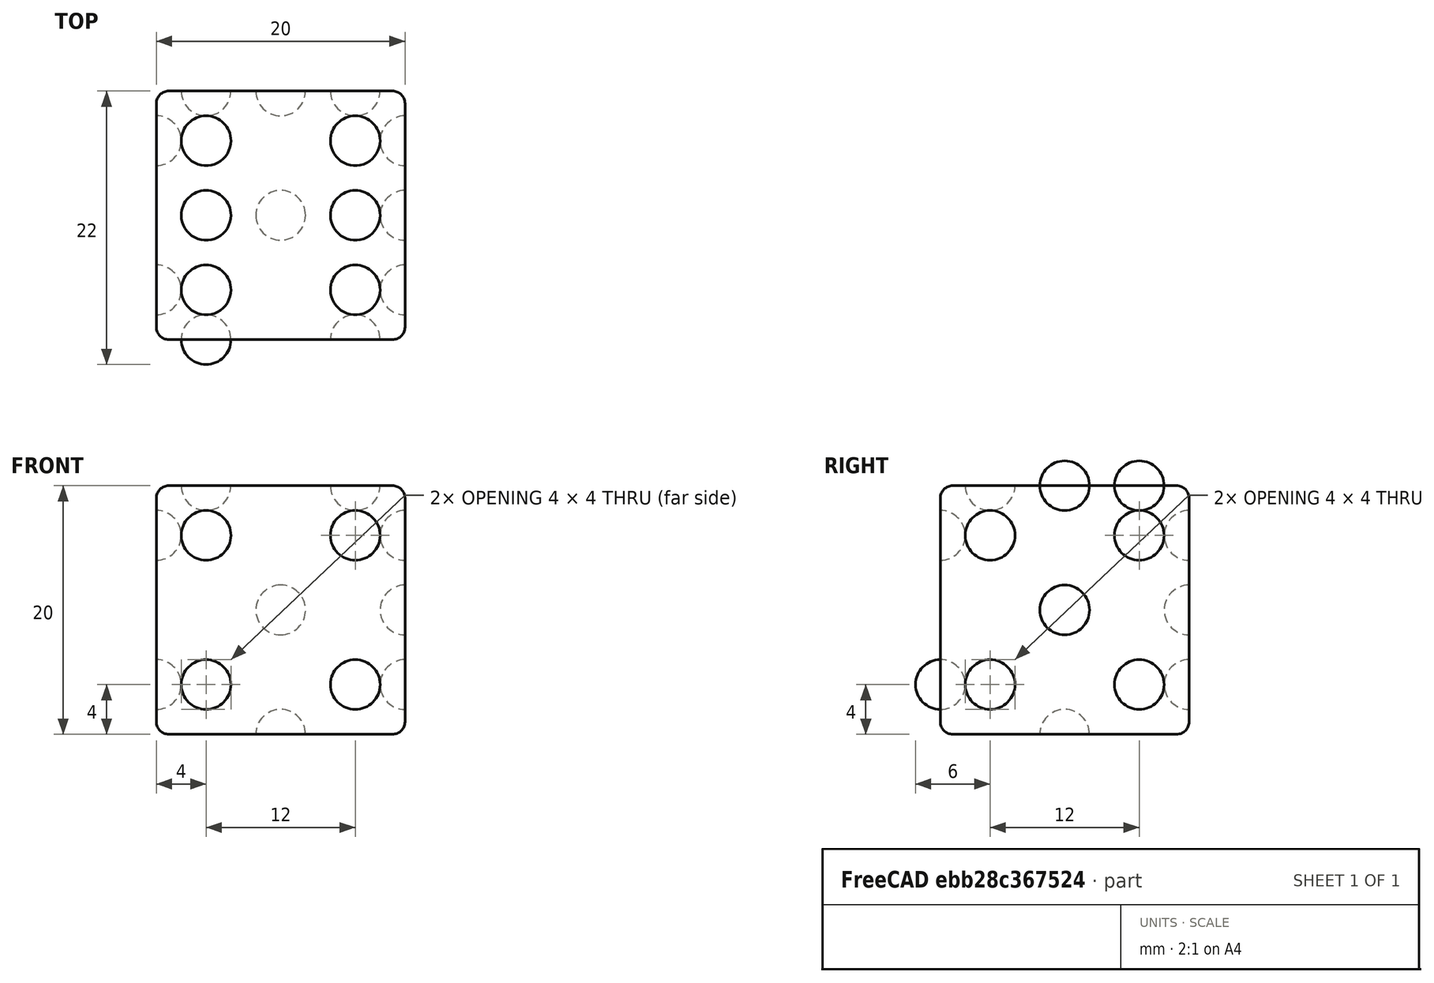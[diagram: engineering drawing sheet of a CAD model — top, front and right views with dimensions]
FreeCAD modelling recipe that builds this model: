
FCSTD DOCUMENT  (FreeCAD 1.0R39319 (Git))
Label: ojt1_t13r02_dado
License: All rights reserved
LicenseURL: https://en.wikipedia.org/wiki/All_rights_reserved
objects: Part::FeaturePython×12, Part::Sphere×10, Part::Cut×10, Part::MultiFuse×4, App::DocumentObjectGroup×3, Part::Box×1, Part::Fillet×1
note: 32 computed .brp shape members not serialized (recipe doc carries the construction recipe); baked Part::Feature solids carry a one-line shape summary decoded from their .brp

FEATURE [Part::Box] Box  label="Cube"
  AttacherType = Attacher::AttachEngine3D
  Height = 20
  Length = 20
  Width = 20
FEATURE [Part::Sphere] Sphere
  Angle1 = -90
  Angle2 = 90
  Angle3 = 360
  AttacherType = Attacher::AttachEngine3D
  Placement = pos=(4,0,4) rot=(0,0,1;0rad)
  Radius = 2
FEATURE [Part::FeaturePython] Array  # Draft array (typed FeaturePython)
  AlwaysSyncPlacement = false
  Angle = 360
  ArrayType = 0
  Axis = (0,0,1)
  Base = -> Sphere
  Center = (0,0,0)
  Count = 6
  ExpandArray = false
  Fuse = false
  IntervalAxis = (0,0,0)
  IntervalX = (6,0,0)
  IntervalY = (0,12,0)
  IntervalZ = (0,0,12)
  NumberCircles = 3
  NumberPolar = 5
  NumberX = 3
  NumberY = 1
  NumberZ = 2
  Placement = pos=(20,20,20) rot=(-0.57735,0.57735,0.57735;4.18879rad)
  PlacementList = 6 placements: [(4,0,4),(4,0,16),(10,0,4),(10,0,16),(16,0,4),(16,0,16)]
  RadialDistance = 50
  ScaleList = (6) [(1,1,1),(1,1,1),(1,1,1),(1,1,1),(1,1,1),(1,1,1)]
  Symmetry = 1
  TangentialDistance = 25
FEATURE [Part::Sphere] Sphere003
  Angle1 = -90
  Angle2 = 90
  Angle3 = 360
  AttacherType = Attacher::AttachEngine3D
  Placement = pos=(4,0,4) rot=(0,0,1;0rad)
  Radius = 2
FEATURE [Part::FeaturePython] Array002  # Draft array (typed FeaturePython)
  AlwaysSyncPlacement = false
  Angle = 360
  ArrayType = 0
  Axis = (0,0,1)
  Base = -> Sphere003
  Center = (0,0,0)
  Count = 4
  ExpandArray = false
  Fuse = false
  IntervalAxis = (0,0,0)
  IntervalX = (12,0,0)
  IntervalY = (0,12,0)
  IntervalZ = (0,0,12)
  NumberCircles = 3
  NumberPolar = 5
  NumberX = 2
  NumberY = 1
  NumberZ = 2
  PlacementList = 4 placements: [(4,0,4),(4,0,16),(16,0,4),(16,0,16)]
  RadialDistance = 50
  ScaleList = (4) [(1,1,1),(1,1,1),(1,1,1),(1,1,1)]
  Symmetry = 1
  TangentialDistance = 25
FEATURE [Part::Sphere] Sphere004
  Angle1 = -90
  Angle2 = 90
  Angle3 = 360
  AttacherType = Attacher::AttachEngine3D
  Placement = pos=(4,0,4) rot=(0,0,1;0rad)
  Radius = 2
FEATURE [Part::FeaturePython] Array003  # Draft array (typed FeaturePython)
  AlwaysSyncPlacement = false
  Angle = 360
  ArrayType = 0
  Axis = (0,0,1)
  Base = -> Sphere004
  Center = (0,0,0)
  Count = 4
  ExpandArray = false
  Fuse = false
  IntervalAxis = (0,0,0)
  IntervalX = (12,0,0)
  IntervalY = (0,12,0)
  IntervalZ = (0,0,12)
  NumberCircles = 3
  NumberPolar = 5
  NumberX = 2
  NumberY = 1
  NumberZ = 2
  Placement = pos=(0,0,0) rot=(0,0,1;1.5708rad)
  PlacementList = 4 placements: [(4,0,4),(4,0,16),(16,0,4),(16,0,16)]
  RadialDistance = 50
  ScaleList = (4) [(1,1,1),(1,1,1),(1,1,1),(1,1,1)]
  Symmetry = 1
  TangentialDistance = 25
FEATURE [Part::Sphere] Sphere009
  Angle1 = -90
  Angle2 = 90
  Angle3 = 360
  AttacherType = Attacher::AttachEngine3D
  Placement = pos=(0,10,10) rot=(0,0,1;0rad)
  Radius = 2
FEATURE [Part::Sphere] Sphere001
  Angle1 = -90
  Angle2 = 90
  Angle3 = 360
  AttacherType = Attacher::AttachEngine3D
  Placement = pos=(4,0,4) rot=(0,0,1;0rad)
  Radius = 2
FEATURE [Part::FeaturePython] Array001  # Draft array (typed FeaturePython)
  AlwaysSyncPlacement = false
  Angle = 360
  ArrayType = 0
  Axis = (0,0,1)
  Base = -> Sphere001
  Center = (0,0,0)
  Count = 4
  ExpandArray = false
  Fuse = false
  IntervalAxis = (0,0,0)
  IntervalX = (12,0,0)
  IntervalY = (0,12,0)
  IntervalZ = (0,0,12)
  NumberCircles = 3
  NumberPolar = 5
  NumberX = 2
  NumberY = 1
  NumberZ = 2
  Placement = pos=(0,0,0) rot=(0,0,1;1.5708rad)
  PlacementList = 4 placements: [(4,0,4),(4,0,16),(16,0,4),(16,0,16)]
  RadialDistance = 50
  ScaleList = (4) [(1,1,1),(1,1,1),(1,1,1),(1,1,1)]
  Symmetry = 1
  TangentialDistance = 25
FEATURE [Part::Sphere] Sphere002
  Angle1 = -90
  Angle2 = 90
  Angle3 = 360
  AttacherType = Attacher::AttachEngine3D
  Placement = pos=(0,10,10) rot=(0,0,1;0rad)
  Radius = 2
FEATURE [Part::MultiFuse] Fusion
  Refine = true
  Shapes = -> [Sphere002,Array001]
FEATURE [Part::Sphere] Sphere006
  Angle1 = -90
  Angle2 = 90
  Angle3 = 360
  AttacherType = Attacher::AttachEngine3D
  Placement = pos=(4,0,4) rot=(0,0,1;0rad)
  Radius = 2
FEATURE [Part::Sphere] Sphere005
  Angle1 = -90
  Angle2 = 90
  Angle3 = 360
  AttacherType = Attacher::AttachEngine3D
  Placement = pos=(0,10,10) rot=(0,0,1;0rad)
  Radius = 2
FEATURE [Part::FeaturePython] Array004  # Draft array (typed FeaturePython)
  AlwaysSyncPlacement = false
  Angle = 360
  ArrayType = 0
  Axis = (0,0,1)
  Base = -> Sphere006
  Center = (0,0,0)
  Count = 4
  ExpandArray = false
  Fuse = false
  IntervalAxis = (0,0,0)
  IntervalX = (12,0,0)
  IntervalY = (0,12,0)
  IntervalZ = (0,0,12)
  NumberCircles = 3
  NumberPolar = 5
  NumberX = 2
  NumberY = 1
  NumberZ = 2
  Placement = pos=(0,0,0) rot=(0,0,1;1.5708rad)
  PlacementList = 4 placements: [(4,0,4),(4,0,16),(16,0,4),(16,0,16)]
  RadialDistance = 50
  ScaleList = (4) [(1,1,1),(1,1,1),(1,1,1),(1,1,1)]
  Symmetry = 1
  TangentialDistance = 25
FEATURE [Part::Sphere] Sphere007
  Angle1 = -90
  Angle2 = 90
  Angle3 = 360
  AttacherType = Attacher::AttachEngine3D
  Placement = pos=(0,10,10) rot=(0,0,1;0rad)
  Radius = 2
FEATURE [Part::Sphere] Sphere008
  Angle1 = -90
  Angle2 = 90
  Angle3 = 360
  AttacherType = Attacher::AttachEngine3D
  Placement = pos=(4,0,4) rot=(0,0,1;0rad)
  Radius = 2
FEATURE [Part::MultiFuse] Fusion002
  Placement = pos=(20,20,0) rot=(0,0,1;1.5708rad)
  Refine = true
  Shapes = -> [Sphere007,Array004]
FEATURE [Part::FeaturePython] Array005  # Draft array (typed FeaturePython)
  AlwaysSyncPlacement = false
  Angle = 360
  ArrayType = 0
  Axis = (0,0,1)
  Base = -> Sphere008
  Center = (0,0,0)
  Count = 4
  ExpandArray = false
  Fuse = false
  IntervalAxis = (0,0,0)
  IntervalX = (12,0,0)
  IntervalY = (0,12,0)
  IntervalZ = (0,0,12)
  NumberCircles = 3
  NumberPolar = 5
  NumberX = 2
  NumberY = 1
  NumberZ = 2
  Placement = pos=(0,0,0) rot=(0,0,1;1.5708rad)
  PlacementList = 4 placements: [(4,0,4),(4,0,16),(16,0,4),(16,0,16)]
  RadialDistance = 50
  ScaleList = (4) [(1,1,1),(1,1,1),(1,1,1),(1,1,1)]
  Symmetry = 1
  TangentialDistance = 25
FEATURE [Part::MultiFuse] Fusion003
  Placement = pos=(20,0,0) rot=(0,0,1;0rad)
  Refine = true
  Shapes = -> [Sphere009,Array005]
FEATURE [Part::MultiFuse] Fusion001
  Placement = pos=(0,0,0) rot=(0,6,0;1.5708rad)
  Refine = true
  Shapes = -> [Sphere005,Array003]
FEATURE [App::DocumentObjectGroup] GrExplode_Fusion001  label="Exploded Fusion001"
FEATURE [Part::FeaturePython] Fusion001_child0  label="Fusion001.0"  # WARN: FeaturePython — macro-defined, semantics opaque (R4)
  Base = -> Fusion001
  FilterType = 1
  Invert = false
  OverrideMaxVal = 0
  WindowFrom = 80
  WindowTo = 100
  items = 0
FEATURE [App::DocumentObjectGroup] GrExplode_Fusion  label="Exploded Fusion"
FEATURE [Part::FeaturePython] Fusion_child1  label="Fusion.1"  # WARN: FeaturePython — macro-defined, semantics opaque (R4)
  Base = -> Fusion
  FilterType = 1
  Invert = false
  OverrideMaxVal = 0
  WindowFrom = 80
  WindowTo = 100
  items = 1
FEATURE [Part::FeaturePython] Fusion_child4  label="Fusion.4"  # WARN: FeaturePython — macro-defined, semantics opaque (R4)
  Base = -> Fusion
  FilterType = 1
  Invert = false
  OverrideMaxVal = 0
  WindowFrom = 80
  WindowTo = 100
  items = 4
FEATURE [Part::FeaturePython] Fusion002_child0  label="Fusion002.0"  # WARN: FeaturePython — macro-defined, semantics opaque (R4)
  Base = -> Fusion002
  FilterType = 1
  Invert = false
  OverrideMaxVal = 0
  WindowFrom = 80
  WindowTo = 100
  items = 0
FEATURE [Part::FeaturePython] Fusion002_child2  label="Fusion002.2"  # WARN: FeaturePython — macro-defined, semantics opaque (R4)
  Base = -> Fusion002
  FilterType = 1
  Invert = false
  OverrideMaxVal = 0
  WindowFrom = 80
  WindowTo = 100
  items = 2
FEATURE [Part::FeaturePython] Fusion002_child3  label="Fusion002.3"  # WARN: FeaturePython — macro-defined, semantics opaque (R4)
  Base = -> Fusion002
  FilterType = 1
  Invert = false
  OverrideMaxVal = 0
  WindowFrom = 80
  WindowTo = 100
  items = 3
FEATURE [Part::Fillet] Fillet
  Base = -> Box
  EdgeLinks = -> Box [Edge1,Edge2,Edge3,Edge4,Edge5,Edge6,Edge7,Edge8,Edge9,Edge10,Edge11,Edge12]
  Edges = 12 edges r=1: [Edge1,Edge2,Edge3,Edge4,Edge5,Edge6,Edge7,Edge8,Edge9,Edge10,Edge11,Edge12]
FEATURE [Part::Cut] Cut
  Base = -> Fillet
  Refine = true
  Tool = -> Array
FEATURE [Part::Cut] Cut001
  Base = -> Cut
  Refine = true
  Tool = -> Array002
FEATURE [Part::Cut] Cut002
  Base = -> Cut001
  Refine = true
  Tool = -> Fusion003
FEATURE [Part::Cut] Cut003
  Base = -> Cut002
  Refine = true
  Tool = -> Sphere008
FEATURE [Part::Cut] Cut004
  Base = -> Cut003
  Refine = true
  Tool = -> Fusion_child4
FEATURE [Part::Cut] Cut005
  Base = -> Cut004
  Refine = true
  Tool = -> Fusion_child1
FEATURE [Part::Cut] Cut006
  Base = -> Cut005
  Refine = true
  Tool = -> Fusion001_child0
FEATURE [Part::Cut] Cut007
  Base = -> Cut006
  Refine = true
  Tool = -> Fusion002_child2
FEATURE [Part::Cut] Cut008
  Base = -> Cut007
  Refine = true
  Tool = -> Fusion002_child0
FEATURE [Part::Cut] Cut009
  Base = -> Cut008
  Refine = true
  Tool = -> Fusion002_child3
FEATURE [App::DocumentObjectGroup] GrExplode_Fusion002  label="Exploded Fusion002"
  Group = -> [Cut009]
